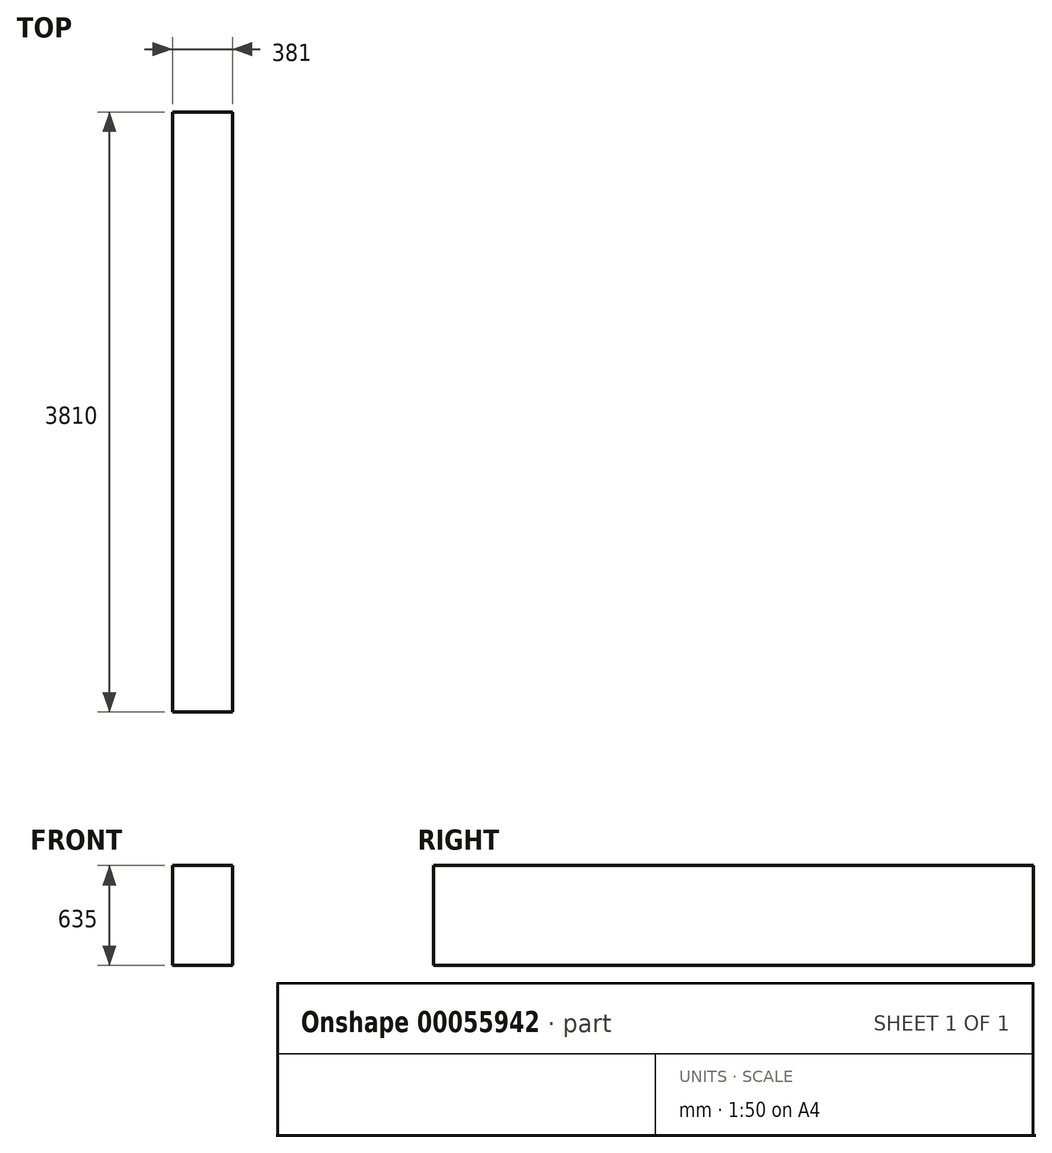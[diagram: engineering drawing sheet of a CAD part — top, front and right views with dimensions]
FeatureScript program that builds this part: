
annotation { "Feature Type Name" : "Feature", "Feature Type Description" : "" }
export const myFeature = defineFeature(function(context is Context, id is Id, definition is map)
    precondition{}
    {
        {
            var Q0;
            Q0=qCreatedBy(makeId("Front.planeOp"),FACE);
            var sketch = newSketch(context, id + "F0", { "sketchPlane" : qUnion([Q0])});
            skLineSegment(sketch, "E0", {"start": v(-239.97, 413.43) * mm, "end": v(141.03, 413.43) * mm});
            skLineSegment(sketch, "E1", {"start": v(141.03, 413.43) * mm, "end": v(141.03, -221.57) * mm});
            skLineSegment(sketch, "E2", {"start": v(141.03, -221.57) * mm, "end": v(-239.97, -221.57) * mm});
            skLineSegment(sketch, "E3", {"start": v(-239.97, -221.57) * mm, "end": v(-239.97, 413.43) * mm});
            skSolve(sketch);
        }
        {
            var Q0;
            Q0=makeQuery(id+"F0.imprint","IMPRINT",FACE,{"disambiguationData":[TD([[makeQuery(id+"F0.imprint","IMPRINT",EDGE,{"derivedFrom":sQuery(id+"F0.wireOp",EDGE,"E0")}),-1.0]])]});
            extrude(context, id + "F1", {"entities" : qUnion([Q0]), "depth" : 3810 * mm});
        }
    });
